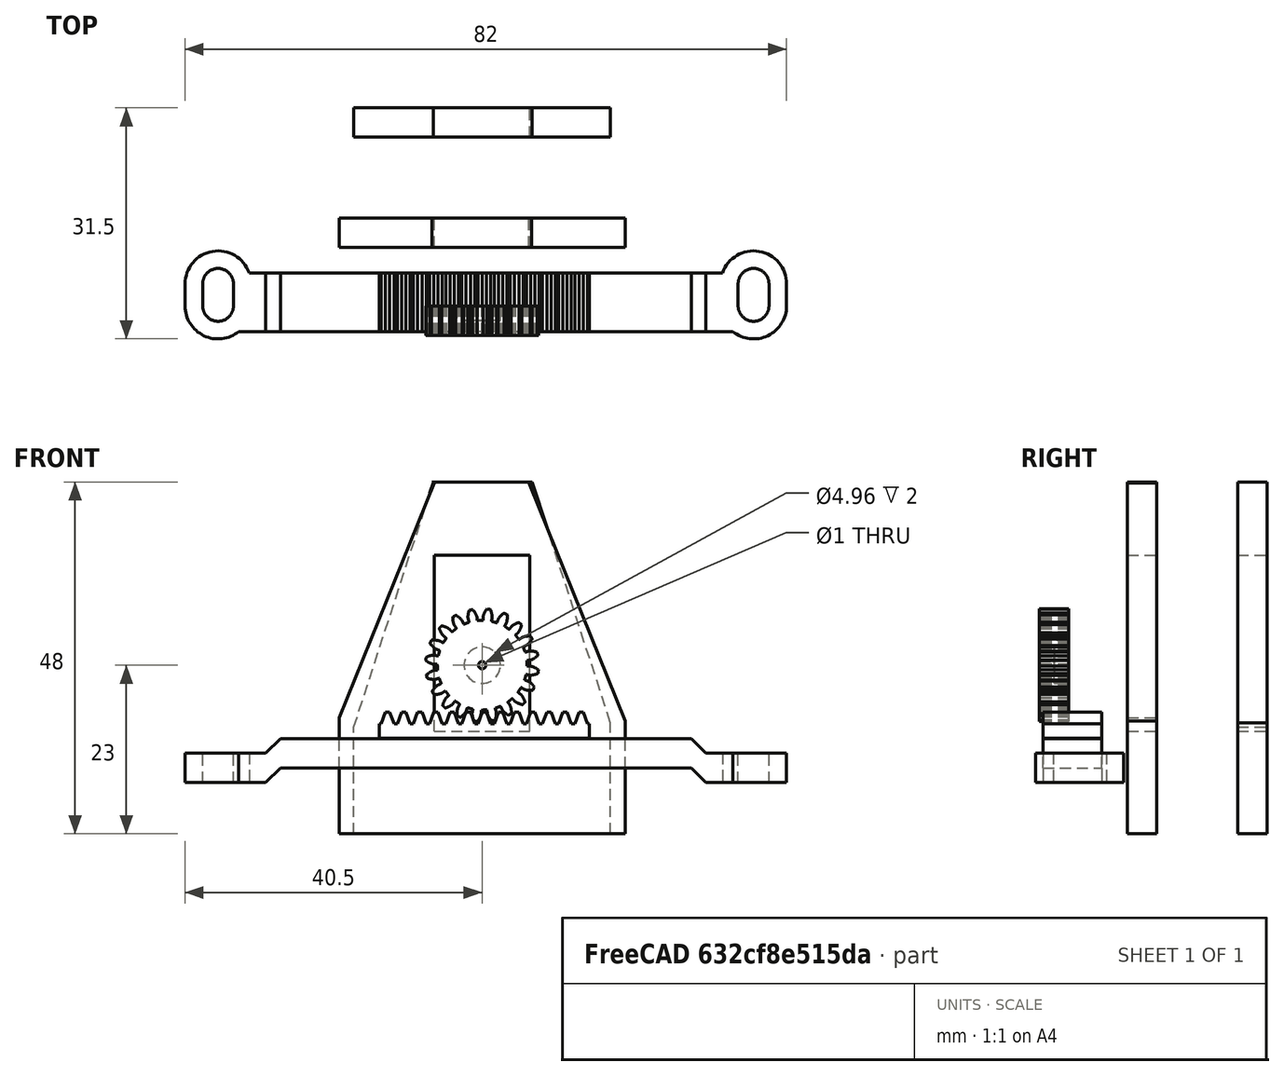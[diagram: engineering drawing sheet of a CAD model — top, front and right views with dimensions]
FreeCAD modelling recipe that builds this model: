
FCSTD DOCUMENT  (FreeCAD 0.20R26651 (Git))
Label: steering
License: All rights reserved
LicenseURL: http://en.wikipedia.org/wiki/All_rights_reserved
objects: Part::Box×19, Part::MultiFuse×11, Part::Cylinder×10, Part::Cut×5, Part::Chamfer×4, Part::FeaturePython×2
note: 51 computed .brp shape members not serialized (recipe doc carries the construction recipe); baked Part::Feature solids carry a one-line shape summary decoded from their .brp

FEATURE [Part::Cylinder] Cylinder  label="Zylinder"
  Angle = 360
  AttacherType = Attacher::AttachEngine3D
  FirstAngle = 0
  Height = 4
  Radius = 2.1
  SecondAngle = 0
FEATURE [Part::Box] Box  label="Würfel"
  AttacherType = Attacher::AttachEngine3D
  Height = 4
  Length = 4.2
  Placement = pos=(-2.1,0,0) rot=(0,0,1;0rad)
  Width = 3
FEATURE [Part::Cylinder] Cylinder001  label="Zylinder001"
  Angle = 360
  AttacherType = Attacher::AttachEngine3D
  FirstAngle = 0
  Height = 4
  Placement = pos=(0,3,0) rot=(0,0,1;0rad)
  Radius = 2.1
  SecondAngle = 0
FEATURE [Part::MultiFuse] Fusion
  Shapes = -> [Cylinder,Box,Cylinder001]
FEATURE [Part::Cylinder] Cylinder002  label="Zylinder002"
  Angle = 360
  AttacherType = Attacher::AttachEngine3D
  FirstAngle = 0
  Height = 4
  Radius = 4.5
  SecondAngle = 0
FEATURE [Part::Box] Box001  label="Würfel001"
  AttacherType = Attacher::AttachEngine3D
  Height = 4
  Length = 9
  Placement = pos=(-4.5,0,0) rot=(0,0,1;0rad)
  Width = 3
FEATURE [Part::Cylinder] Cylinder003  label="Zylinder003"
  Angle = 360
  AttacherType = Attacher::AttachEngine3D
  FirstAngle = 0
  Height = 4
  Placement = pos=(0,3,0) rot=(0,0,1;0rad)
  Radius = 4.5
  SecondAngle = 0
FEATURE [Part::MultiFuse] Fusion001
  Shapes = -> [Cylinder002,Box001,Cylinder003]
FEATURE [Part::Cut] Cut
  Base = -> Fusion001
  Placement = pos=(4.5,0,0) rot=(0,0,1;0rad)
  Tool = -> Fusion
FEATURE [Part::Cylinder] Cylinder004  label="Zylinder004"
  Angle = 360
  AttacherType = Attacher::AttachEngine3D
  FirstAngle = 0
  Height = 4
  Radius = 2.1
  SecondAngle = 0
FEATURE [Part::Box] Box002  label="Würfel002"
  AttacherType = Attacher::AttachEngine3D
  Height = 4
  Length = 4.2
  Placement = pos=(-2.1,0,0) rot=(0,0,1;0rad)
  Width = 3
FEATURE [Part::Cylinder] Cylinder005  label="Zylinder005"
  Angle = 360
  AttacherType = Attacher::AttachEngine3D
  FirstAngle = 0
  Height = 4
  Placement = pos=(0,3,0) rot=(0,0,1;0rad)
  Radius = 2.1
  SecondAngle = 0
FEATURE [Part::MultiFuse] Fusion002
  Shapes = -> [Cylinder004,Box002,Cylinder005]
FEATURE [Part::Cylinder] Cylinder006  label="Zylinder006"
  Angle = 360
  AttacherType = Attacher::AttachEngine3D
  FirstAngle = 0
  Height = 4
  Placement = pos=(0,3,0) rot=(0,0,1;0rad)
  Radius = 4.5
  SecondAngle = 0
FEATURE [Part::Box] Box003  label="Würfel003"
  AttacherType = Attacher::AttachEngine3D
  Height = 4
  Length = 9
  Placement = pos=(-4.5,0,0) rot=(0,0,1;0rad)
  Width = 3
FEATURE [Part::Cylinder] Cylinder007  label="Zylinder007"
  Angle = 360
  AttacherType = Attacher::AttachEngine3D
  FirstAngle = 0
  Height = 4
  Radius = 4.5
  SecondAngle = 0
FEATURE [Part::MultiFuse] Fusion003
  Shapes = -> [Cylinder007,Box003,Cylinder006]
FEATURE [Part::Cut] Cut001
  Base = -> Fusion003
  Placement = pos=(77.5,0,0) rot=(0,0,1;0rad)
  Tool = -> Fusion002
FEATURE [Part::Box] Box004  label="Würfel004"
  AttacherType = Attacher::AttachEngine3D
  Height = 4
  Length = 6
  Placement = pos=(7,-3.5,0) rot=(0,0,1;0rad)
  Width = 8
FEATURE [Part::Box] Box005  label="Würfel005"
  AttacherType = Attacher::AttachEngine3D
  Height = 4
  Length = 6
  Placement = pos=(69,-3.5,0) rot=(0,0,1;0rad)
  Width = 8
FEATURE [Part::Box] Box006  label="Würfel006"
  AttacherType = Attacher::AttachEngine3D
  Height = 4
  Length = 60
  Placement = pos=(11,-3.5,2) rot=(0,0,1;0rad)
  Width = 8
FEATURE [Part::Chamfer] Chamfer
  Base = -> Box006
  Edges = 1 edges r=2: [Edge2]
FEATURE [Part::Chamfer] Chamfer001
  Base = -> Box004
  Edges = 1 edges r=2: [Edge8]
FEATURE [Part::Chamfer] Chamfer002
  Base = -> Box005
  Edges = 1 edges r=2: [Edge4]
FEATURE [Part::Chamfer] Chamfer003
  Base = -> Chamfer
  Edges = 1 edges r=2: [Edge15]
FEATURE [Part::MultiFuse] Fusion004
  Shapes = -> [Chamfer001,Chamfer002,Chamfer003]
FEATURE [Part::MultiFuse] Fusion005
  Shapes = -> [Cut,Cut001,Fusion004]
FEATURE [Part::Cylinder] Cylinder008  label="Zylinder008"
  Angle = 360
  AttacherType = Attacher::AttachEngine3D
  FirstAngle = 0
  Height = 4
  Placement = pos=(0,0,0) rot=(1,0,0;1.5708rad)
  Radius = 0.5
  SecondAngle = 0
FEATURE [Part::Cylinder] Cylinder009  label="Zylinder009"
  Angle = 360
  AttacherType = Attacher::AttachEngine3D
  FirstAngle = 0
  Height = 2
  Placement = pos=(0,0,0) rot=(1,0,0;1.5708rad)
  Radius = 2.48
  SecondAngle = 0
FEATURE [Part::FeaturePython] involutegear  # WARN: FeaturePython — macro-defined, semantics opaque (R4)
  AttacherType = Attacher::AttachEngine3D
  Placement = pos=(0,0,0) rot=(1,0,0;1.5708rad)
  backlash = 0
  beta = 0
  clearance = 0.25
  da = 15.4
  df = 12.25
  double_helix = false
  dw = 14
  head = 0
  height = 4
  module = 0.7
  numpoints = 6
  pressure_angle = 20
  properties_from_tool = false
  reversed_backlash = false
  shift = 0
  simple = false
  teeth = 20
  transverse_pitch = 2.19911
  undercut = false
  version = 0.0.3
FEATURE [Part::FeaturePython] involuterack  label="rack"  # WARN: FeaturePython — macro-defined, semantics opaque (R4)
  AttacherType = Attacher::AttachEngine3D
  Placement = pos=(54,4.5,8.9) rot=(0.57735,-0.57735,0.57735;2.0944rad)
  add_endings = true
  beta = 0
  clearance = 0.25
  double_helix = false
  head = 0
  height = 8
  module = 0.7
  pressure_angle = 20
  properties_from_tool = true
  simplified = false
  teeth = 13
  thickness = 2
  transverse_pitch = 2.19911
  version = 0.0.3
FEATURE [Part::MultiFuse] Fusion006
  Shapes = -> [Cylinder009,Cylinder008]
FEATURE [Part::Cut] Cut002  label="gear"
  Base = -> involutegear
  Placement = pos=(40.5,0,16) rot=(0,1,0;0.113446rad)
  Tool = -> Fusion006
FEATURE [Part::Box] Box007  label="Würfel007"
  AttacherType = Attacher::AttachEngine3D
  Height = 14
  Length = 39
  Width = 4
FEATURE [Part::Box] Box008  label="Würfel008"
  AttacherType = Attacher::AttachEngine3D
  Height = 34
  Length = 13
  Placement = pos=(0,0,14) rot=(0,0,1;0rad)
  Width = 4
FEATURE [Part::Box] Box009  label="Würfel009"
  AttacherType = Attacher::AttachEngine3D
  Height = 34
  Length = 13
  Placement = pos=(26,0,14) rot=(0,0,1;0rad)
  Width = 4
FEATURE [Part::Box] Box010  label="Würfel010"
  AttacherType = Attacher::AttachEngine3D
  Height = 10
  Length = 13
  Placement = pos=(13,0,38) rot=(0,0,1;0rad)
  Width = 4
FEATURE [Part::MultiFuse] Fusion007
  Shapes = -> [Box007,Box008,Box009,Box010]
FEATURE [Part::Box] Box011  label="Würfel011"
  AttacherType = Attacher::AttachEngine3D
  Height = 43
  Length = 16
  Placement = pos=(-18,0,14) rot=(0,1,0;0.383972rad)
  Width = 4
FEATURE [Part::Box] Box012  label="Würfel012"
  AttacherType = Attacher::AttachEngine3D
  Height = 43
  Length = 16
  Placement = pos=(42,0,8) rot=(0,-1,0;0.383972rad)
  Width = 4
FEATURE [Part::MultiFuse] Fusion008
  Shapes = -> [Box011,Box012]
FEATURE [Part::Cut] Cut003
  Base = -> Fusion007
  Placement = pos=(21,8,-7) rot=(0,0,1;0rad)
  Tool = -> Fusion008
FEATURE [Part::Box] Box013  label="Würfel013"
  AttacherType = Attacher::AttachEngine3D
  Height = 14
  Length = 35
  Placement = pos=(2,0,0) rot=(0,0,1;0rad)
  Width = 4
FEATURE [Part::Box] Box014  label="Würfel014"
  AttacherType = Attacher::AttachEngine3D
  Height = 34
  Length = 11
  Placement = pos=(2,0,14) rot=(0,0,1;0rad)
  Width = 4
FEATURE [Part::Box] Box015  label="Würfel015"
  AttacherType = Attacher::AttachEngine3D
  Height = 34
  Length = 11
  Placement = pos=(26,0,14) rot=(0,0,1;0rad)
  Width = 4
FEATURE [Part::Box] Box016  label="Würfel016"
  AttacherType = Attacher::AttachEngine3D
  Height = 10
  Length = 13
  Placement = pos=(13,0,38) rot=(0,0,1;0rad)
  Width = 4
FEATURE [Part::MultiFuse] Fusion009
  Shapes = -> [Box013,Box014,Box015,Box016]
FEATURE [Part::Box] Box017  label="Würfel017"
  AttacherType = Attacher::AttachEngine3D
  Height = 43
  Length = 16
  Placement = pos=(-15,0,14) rot=(0,1,0;0.314159rad)
  Width = 4
FEATURE [Part::Box] Box018  label="Würfel018"
  AttacherType = Attacher::AttachEngine3D
  Height = 43
  Length = 16
  Placement = pos=(39,0,9) rot=(0,-1,0;0.314159rad)
  Width = 4
FEATURE [Part::MultiFuse] Fusion010
  Shapes = -> [Box017,Box018]
FEATURE [Part::Cut] Cut004
  Base = -> Fusion009
  Placement = pos=(21,23,-7) rot=(0,0,1;0rad)
  Tool = -> Fusion010
